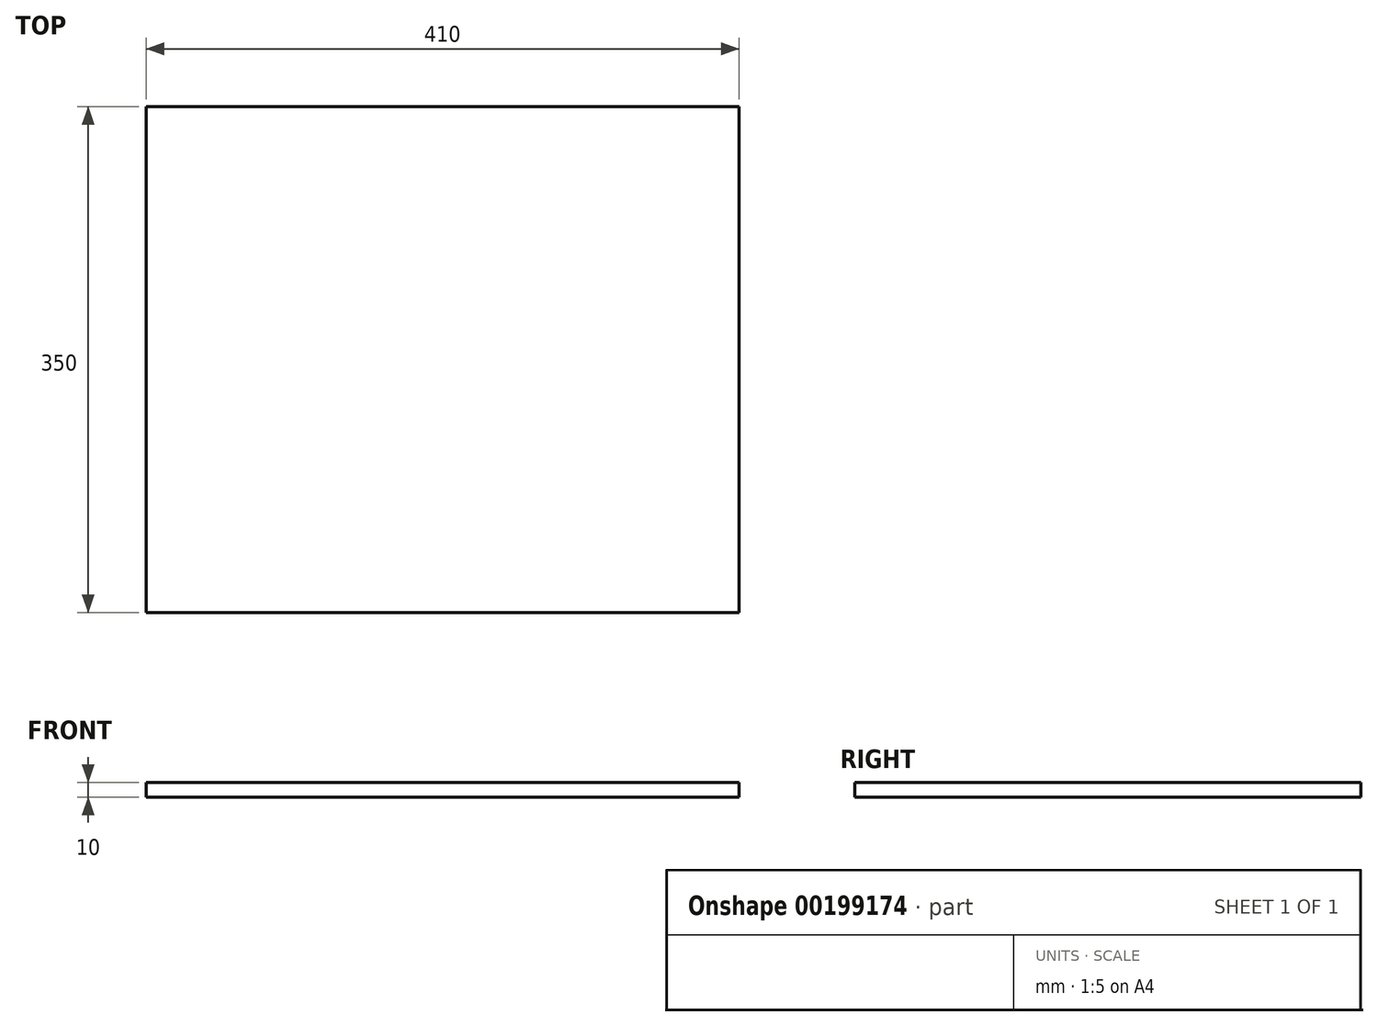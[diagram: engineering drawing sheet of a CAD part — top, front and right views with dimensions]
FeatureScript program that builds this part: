
annotation { "Feature Type Name" : "Feature", "Feature Type Description" : "" }
export const myFeature = defineFeature(function(context is Context, id is Id, definition is map)
    precondition{}
    {
        {
            var Q0;
            Q0=qCreatedBy(makeId("Top.planeOp"),FACE);
            var sketch = newSketch(context, id + "F0", { "sketchPlane" : qUnion([Q0])});
            skLineSegment(sketch, "E0.bottom", {"start": v(-70.96, 65.05) * mm, "end": v(339.04, 65.05) * mm});
            skLineSegment(sketch, "E0.top", {"start": v(-70.96, -284.95) * mm, "end": v(339.04, -284.95) * mm});
            skLineSegment(sketch, "E0.left", {"start": v(-70.96, 65.05) * mm, "end": v(-70.96, -284.95) * mm});
            skLineSegment(sketch, "E0.right", {"start": v(339.04, 65.05) * mm, "end": v(339.04, -284.95) * mm});
            skSolve(sketch);
        }
        {
            var Q0;
            Q0=qSketchRegion(id+"F0",true);
            extrude(context, id + "F1", {"entities" : qUnion([Q0]), "depth" : 10 * mm});
        }
    });
